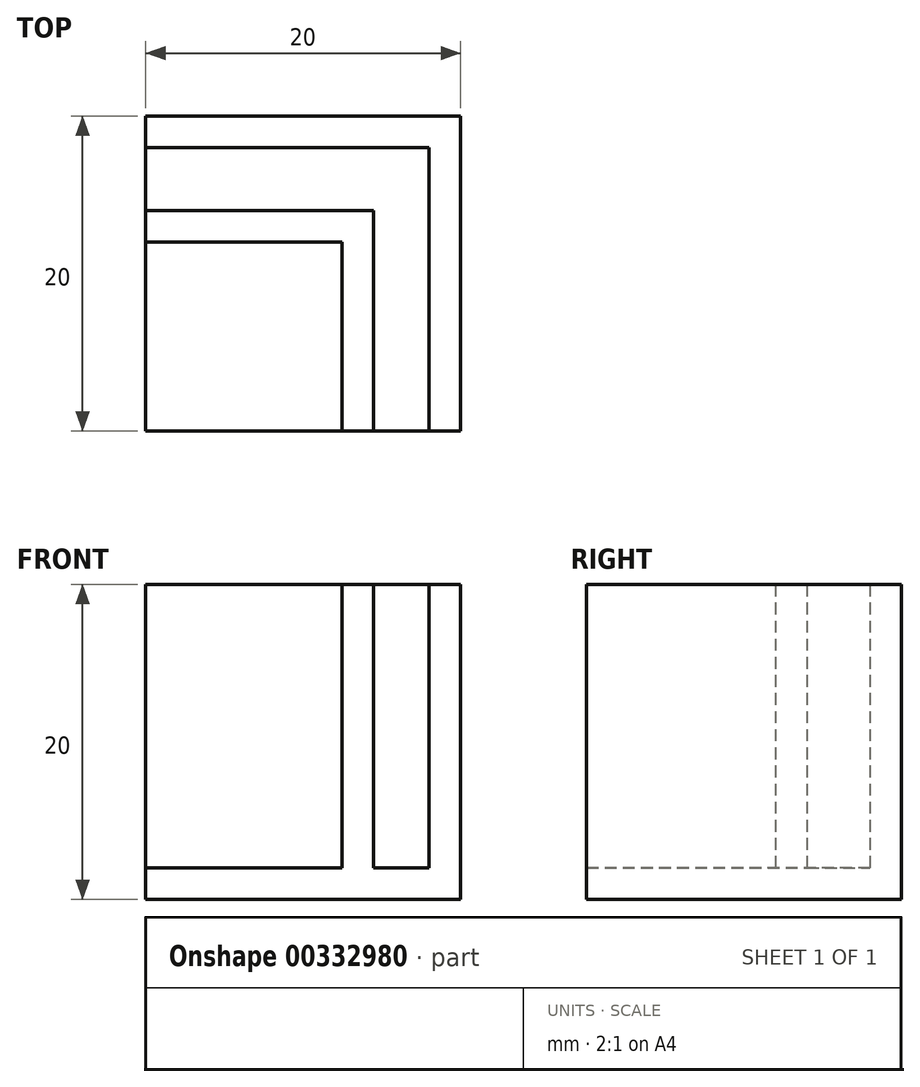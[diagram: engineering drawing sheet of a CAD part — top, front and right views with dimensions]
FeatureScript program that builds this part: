
annotation { "Feature Type Name" : "Feature", "Feature Type Description" : "" }
export const myFeature = defineFeature(function(context is Context, id is Id, definition is map)
    precondition{}
    {
        {
            var Q0;
            Q0=qCreatedBy(makeId("Top.planeOp"),FACE);
            var sketch = newSketch(context, id + "F0", { "sketchPlane" : qUnion([Q0])});
            skLineSegment(sketch, "E0.bottom", {"start": v(-5.86, -2.23) * mm, "end": v(14.14, -2.23) * mm});
            skLineSegment(sketch, "E0.top", {"start": v(-5.86, 17.77) * mm, "end": v(14.14, 17.77) * mm});
            skLineSegment(sketch, "E0.left", {"start": v(-5.86, -2.23) * mm, "end": v(-5.86, 17.77) * mm});
            skLineSegment(sketch, "E0.right", {"start": v(14.14, -2.23) * mm, "end": v(14.14, 17.77) * mm});
            skSolve(sketch);
        }
        {
            var Q0;
            Q0=makeQuery(id+"F0.imprint","IMPRINT",FACE,{"disambiguationData":[TD([[makeQuery(id+"F0.imprint","IMPRINT",EDGE,{"derivedFrom":sQuery(id+"F0.wireOp",EDGE,"E0.bottom")}),1.0]])]});
            extrude(context, id + "F1", {"entities" : qUnion([Q0]), "depth" : 2 * mm});
        }
        {
            var Q0;
            Q0=makeQuery(id+"F1.opExtrude","CAP_FACE",FACE,{"disambiguationData":[OSD([sQuery(id+"F0.wireOp",EDGE,"E0.bottom"),sQuery(id+"F0.wireOp",EDGE,"E0.top"),sQuery(id+"F0.wireOp",EDGE,"E0.left"),sQuery(id+"F0.wireOp",EDGE,"E0.right")])],"isStart":false});
            var sketch = newSketch(context, id + "F2", { "sketchPlane" : qUnion([Q0])});
            skLineSegment(sketch, "E1", {"start": v(-5.86, 17.77) * mm, "end": v(-5.86, 15.77) * mm});
            skLineSegment(sketch, "E2", {"start": v(-5.86, 15.77) * mm, "end": v(12.14, 15.77) * mm});
            skLineSegment(sketch, "E3", {"start": v(12.14, 15.77) * mm, "end": v(12.14, -2.23) * mm});
            skSolve(sketch);
        }
        {
            var Q0;
            Q0=makeQuery(id+"F2.imprint","IMPRINT",FACE,{"disambiguationData":[TD([[makeQuery(id+"F2.imprint","IMPRINT",EDGE,{"derivedFrom":sQuery(id+"F2.wireOp",EDGE,"E1")}),-1.0]])]});
            extrude(context, id + "F3", {"entities" : qUnion([Q0]), "operationType" : NewBodyOperationType.ADD, "depth" : 18 * mm});
        }
        {
            var Q0;
            Q0=makeQuery(id+"F1.opExtrude","CAP_FACE",FACE,{"disambiguationData":[OSD([sQuery(id+"F0.wireOp",EDGE,"E0.bottom"),sQuery(id+"F0.wireOp",EDGE,"E0.top"),sQuery(id+"F0.wireOp",EDGE,"E0.left"),sQuery(id+"F0.wireOp",EDGE,"E0.right")])],"isStart":false});
            var sketch = newSketch(context, id + "F4", { "sketchPlane" : qUnion([Q0])});
            skLineSegment(sketch, "E4", {"start": v(-5.86, 15.77) * mm, "end": v(-5.86, 11.77) * mm});
            skLineSegment(sketch, "E5", {"start": v(-5.86, 11.77) * mm, "end": v(8.14, 11.77) * mm});
            skLineSegment(sketch, "E6", {"start": v(8.61, -2.23) * mm, "end": v(6.61, -2.23) * mm});
            skLineSegment(sketch, "E7", {"start": v(-5.86, 9.77) * mm, "end": v(-5.86, 11.77) * mm});
            skLineSegment(sketch, "E8", {"start": v(8.61, -2.23) * mm, "end": v(8.61, 11.77) * mm});
            skLineSegment(sketch, "E9", {"start": v(8.61, 11.77) * mm, "end": v(8.14, 11.77) * mm});
            skLineSegment(sketch, "E10", {"start": v(6.61, -2.23) * mm, "end": v(6.61, 9.77) * mm});
            skLineSegment(sketch, "E11", {"start": v(6.61, 9.77) * mm, "end": v(-5.86, 9.77) * mm});
            skSolve(sketch);
        }
        {
            var Q0;
            Q0=makeQuery(id+"F4.imprint","IMPRINT",FACE,{"disambiguationData":[TD([[makeQuery(id+"F4.imprint","IMPRINT",EDGE,{"derivedFrom":sQuery(id+"F4.wireOp",EDGE,"E5")}),-1.0]])]});
            extrude(context, id + "F5", {"entities" : qUnion([Q0]), "operationType" : NewBodyOperationType.ADD, "depth" : 18 * mm});
        }
    });
